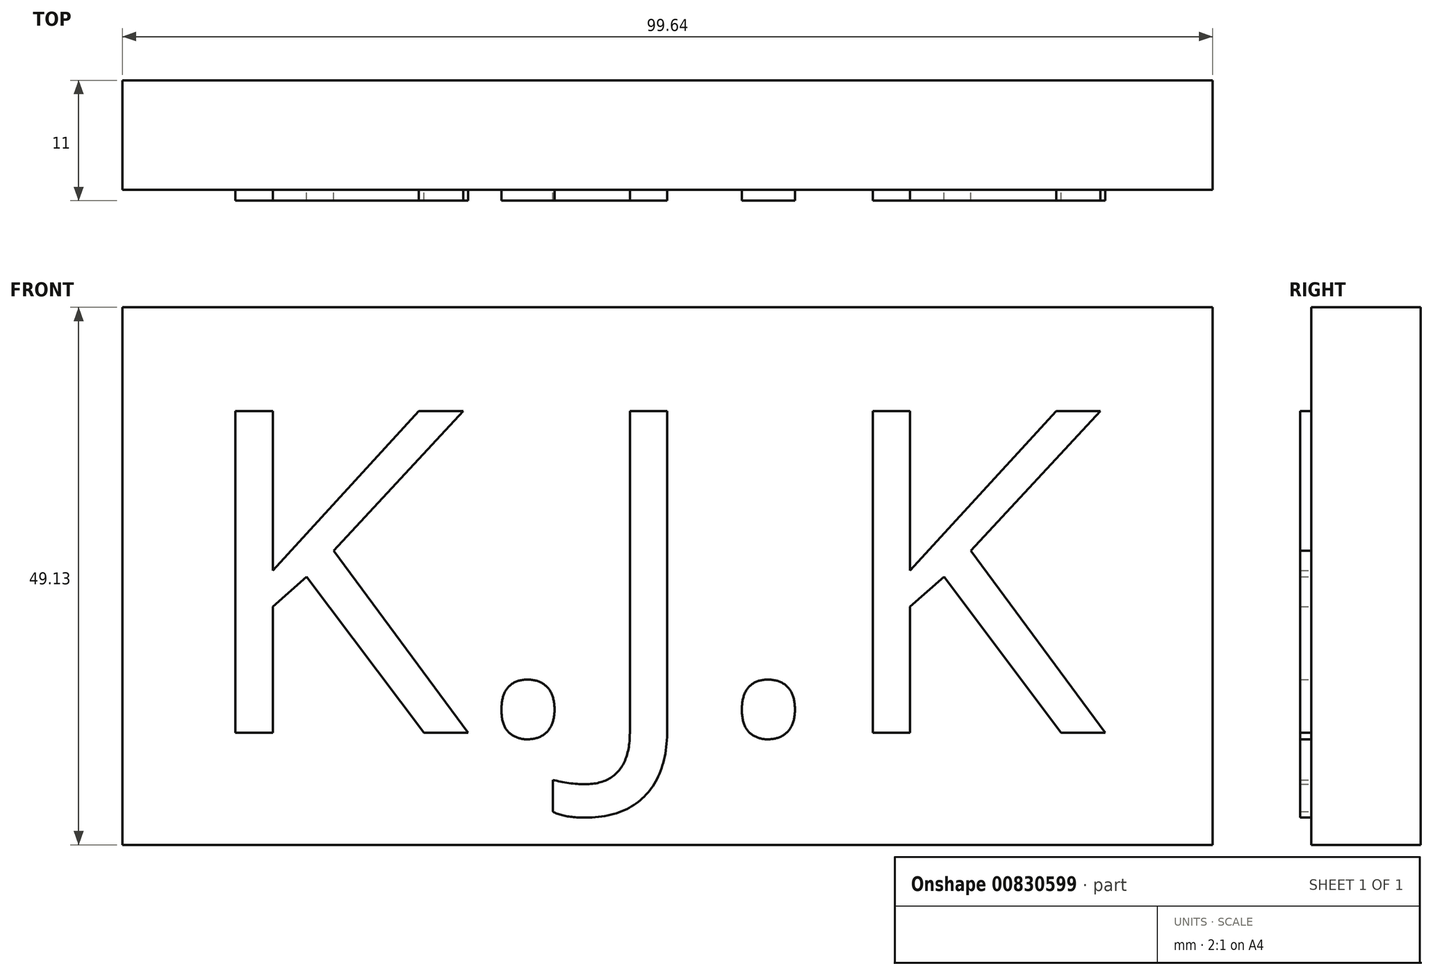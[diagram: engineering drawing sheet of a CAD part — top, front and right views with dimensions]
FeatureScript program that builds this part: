
annotation { "Feature Type Name" : "Feature", "Feature Type Description" : "" }
export const myFeature = defineFeature(function(context is Context, id is Id, definition is map)
    precondition{}
    {
        {
            var Q0;
            Q0=qCreatedBy(makeId("Front.planeOp"),FACE);
            var sketch = newSketch(context, id + "F0", { "sketchPlane" : qUnion([Q0])});
            skLineSegment(sketch, "E0.bottom", {"start": v(0, 0) * mm, "end": v(99.64, 0) * mm});
            skLineSegment(sketch, "E0.top", {"start": v(0, 49.13) * mm, "end": v(99.64, 49.13) * mm});
            skLineSegment(sketch, "E0.left", {"start": v(0, 0) * mm, "end": v(0, 49.13) * mm});
            skLineSegment(sketch, "E0.right", {"start": v(99.64, 0) * mm, "end": v(99.64, 49.13) * mm});
            skSolve(sketch);
        }
        {
            var Q0;
            Q0=makeQuery(id+"F0.imprint","IMPRINT",FACE,{"disambiguationData":[TD([[makeQuery(id+"F0.imprint","IMPRINT",EDGE,{"derivedFrom":sQuery(id+"F0.wireOp",EDGE,"E0.bottom")}),1.0]])]});
            extrude(context, id + "F1", {"entities" : qUnion([Q0]), "depth" : 10 * mm, "offsetDistance" : 25.4 * mm});
        }
        {
            var Q0;
            Q0=makeQuery(id+"F1.opExtrude","CAP_FACE",FACE,{"disambiguationData":[OSD([sQuery(id+"F0.wireOp",EDGE,"E0.bottom"),sQuery(id+"F0.wireOp",EDGE,"E0.top"),sQuery(id+"F0.wireOp",EDGE,"E0.left"),sQuery(id+"F0.wireOp",EDGE,"E0.right")])],"isStart":false});
            var sketch = newSketch(context, id + "F2", { "sketchPlane" : qUnion([Q0])});
            skText(sketch, "E1", { "text": "K.J.K", "fontName": "OpenSans-Regular.ttf"});
            const initialGuessF2  = {"E1": [0.00628, 0.01023, 1, 0, 0.02968]};
            skSetInitialGuess(sketch, initialGuessF2);
            skSolve(sketch);
        }
        {
            var Q0;
            Q0 = qSketchRegion(id + "F2", true);
            extrude(context, id + "F3", {"entities" : qUnion([Q0]), "operationType" : NewBodyOperationType.ADD, "depth" : 1 * mm, "offsetDistance" : 25.4 * mm});
        }
    });
